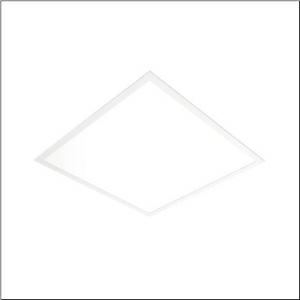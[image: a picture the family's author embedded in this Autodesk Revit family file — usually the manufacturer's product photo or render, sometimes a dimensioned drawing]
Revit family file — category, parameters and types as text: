
# Revit family: apollon_41_51mh11wd2n43
name_source: partatom
category: Lighting Fixtures
units: mm (PartAtom-declared; Revit-internal decimal feet)

## family parameters
Cut with Voids When Loaded = No
Host = Face
Light Source = No
Part Type = Normal
Room Calculation Point = No
Round Connector Dimension = Use Diameter
Shared = No

## types (1)
- --- (1 x LED, 3450 lm, 28.5 W, 6500K)
    Apparent Load = 29 VA
    CIE Flux Codes = 61 87 97 100 100
    Color Rendering = 80
    Color Temperature = 6500K
    Default Elevation = 1800 mm
    Description = Apollon 41, office luminaire, primary optical cover: prismatic diffuser, of PS, light emission: direct distribution, primary light characteristic: symmetric, installation type: lay-in mounting, LED, rated luminous flux: 3.500lm, luminous efficacy: 123lm/W, light colour: 840/865, colour temperature: 4000/6500K, control gear: DALI 2, with terminal, 5-pole, mains connection: 220..240V, AC/DC, 0/50..60Hz, suitable for self-contained emergency lighting element 58DB00B013A with integrated self-test function according to EN 60598-2-22, housing, of aluminium section, traffic white (RAL 9016), module: M625, length: 620mm, width: 620mm, height: 60mm, recess depth: 180mm, housing upper side, of sheet steel, protection rating (complete): IP20, protection rating (lamp compartment, on room side): IP40, insulation class (complete): insulation class II (safety insulation), certification: CE, ENEC, impact resistance: IK03, permissible operating ambient temperature: -25..+40°C, packaging unit: 1 piece
    Height = 0 mm  [stored 0 ft]
    Lamp = 1 x LED
    Lamp Light Flux = 3450 lm
    Lamp Power = 28.5 W
    Lamp count = 1
    Length = 620 mm
    Luminous efficacy = 121 lm/W
    Manufacturer = Siteco
    ModVariant = No
    Model = 51MH11WD2N43
    Mounting Place = Ceiling
    Mounting Type = Recessed
    Number of Poles = 1
    OnlyDefault = Yes
    Power Factor = 1
    Product Name = Apollon 41
    Product group = office luminaire | ceiling recessed
    ProductGroupID = 400
    Protection Class = Protection class II
    Protection Degree = IP 20
    RLX_Detail_Level = 1
    RLX_Emergency_Light_Flux = 0 lm
    RLX_Emergency_Type = 0
    RLX_Emergency_Type_DB = No
    RlxData = <blob elided: 12617 chars, md5=5e8cc383>
    Socket = socket
    Standby Power = 0 W
    System Light Flux = 3450 lm
    System Power = 29 W
    Type Comments = individual setting
    Type Image = l_1291024.jpg
    URL = http://relux.com
    VarID = @adj_084337
    Voltage = 0 V
    Weight = 0.00 kg
    Width = 620 mm

note: [stored X ft] marks values corroborated as IEEE doubles in the binary element streams (Revit-internal decimal feet)

## geometry (parser evidence)
native form markers: Sweep x9
no freeform markers — native parametric forms only
